# Revit family: Faucet-Kitchen_Sink-KOHLER-Evoke-K-6331
name_source: partatom
category: Plumbing Fixtures
revit_build: Autodesk Revit 2015 (Build: 20140606_1530(x64)
units: mm (PartAtom-declared; Revit-internal decimal feet)

## types (2) — shared parameters
ADA Compliant = Yes
Assembly Code = D2020
CW Connection = Yes
Date Modified = 10/07/2017
Default Elevation = 36"
Description = Evoke Single-hole kitchen sink faucet with 9inch pull-out spout
Flow Rate = 2 GPM
HW Connection = Yes
Height = 12"
Inlet Connector = Inlet Connection
Length = 10 21/32"
Manufacturer = KOHLER Co.
MasterFormat 1995 = 15410
MasterFormat 2004 = 22.41.39
Material = Premium Metal Construction
Outlet Connector = Outlet Connection
Pressure = 60.00 psi
Product Documentation Link = http://www.us.kohler.com
Product Name = Evoke
Product Page URL = http://www.us.kohler.com
Spout Reach = 9"
URL = https://www.us.kohler.com
Vent Connection = No
Waste Connection = No
Width = 4 7/32"

## per-type parameters (varying)
| type | Finish | Model | Type |
| CP-Polished Chrome | Kohler-Metal-CP-Polished_Chrome | K-6331-CP | 1 |
| VS-Vibrant Stainless | Kohler-Metal-VS-Vibrant_Stainless | K-6331-VS | 2 |

## geometry (parser evidence)
native form markers: Sweep x5
no freeform markers — native parametric forms only
